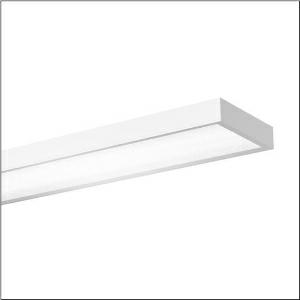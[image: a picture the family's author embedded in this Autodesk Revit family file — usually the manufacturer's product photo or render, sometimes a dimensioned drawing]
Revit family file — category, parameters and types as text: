
# Revit family: sport_31_51hs12dd4jca
name_source: partatom
category: Lighting Fixtures
units: mm (PartAtom-declared; Revit-internal decimal feet)

## family parameters
Cut with Voids When Loaded = No
Host = Face
Light Source = No
Part Type = Normal
Room Calculation Point = No
Round Connector Dimension = Use Diameter
Shared = No

## types (1)
- --- (1 x LED, 19720 lm, 146.2 W, 4000K)
    Apparent Load = 146 VA
    CIE Flux Codes = 65 89 97 100 100
    Color Rendering = 80
    Color Temperature = 4000K
    Default Elevation = 1800 mm
    Description = Sport 31, LED high bay luminaire, primary light control with reflector, of sheet steel, primary anti-glare with prismatic structure, of PC, primary optical cover: cover panel, of PC, light emission: direct distribution, primary light characteristic: symmetric, installation type: suspended mounting, recessed, surface-mounted, LED, rated luminous flux: 20.000lm, luminous efficacy: 137lm/W, light colour: 840, colour temperature: 4000K, control gear: DALI 2, with terminal, 5-pole, max. 2.5mm², mains connection: 220..240V, AC/DC, 50/60Hz, rated input power: 146W, housing, of sheet steel, traffic white (RAL 9016), length: 1.540mm, width: 415mm, height: 95mm, protection rating (complete): IP20, protection rating (lamp compartment, on room side): IP50, insulation class (complete): insulation class I (protective earthing), certification: CE, ENEC, UKCA, ball protection: ball impact resistant with ceiling mounting or chain suspension, impact resistance: IK08, permissible operating ambient temperature: -20..+35°C, standard: DIN 18032-3, EN 60598-2-22, packaging unit: 1 piece
    Height = 100 mm  [stored 0.328084 ft]
    Lamp = 1 x LED
    Lamp Light Flux = 19720 lm
    Lamp Power = 146.2 W
    Lamp count = 1
    Length = 1500 mm
    Luminous efficacy = 135 lm/W
    Manufacturer = Siteco
    ModVariant = No
    Model = 51HS12DD4JCA
    Mounting Place = Ceiling
    Mounting Type = Pendant
    Number of Poles = 1
    OnlyDefault = Yes
    Power Factor = 1
    Product Name = Sport 31
    Product group = LED high bay luminaire
    ProductGroupID = 903
    Protection Class = Protection class I
    Protection Degree = IP 20
    RLX_Detail_Level = 1
    RLX_Emergency_Light_Flux = 0 lm
    RLX_Emergency_Type = 0
    RLX_Emergency_Type_DB = No
    RlxData = <blob elided: 24129 chars, md5=a3e19410>
    Socket = socket
    Standby Power = 0 W
    System Light Flux = 19719 lm
    System Power = 146 W
    Type Comments = factory setting: luminous flux: 100 % | dim-lin: 254 | 610 mA
    Type Image = l_1006829.jpg
    URL = http://relux.com
    VarID = @adj_197098
    Voltage = 0 V
    Weight = 0.00 kg
    Width = 415 mm

note: [stored X ft] marks values corroborated as IEEE doubles in the binary element streams (Revit-internal decimal feet)

## geometry (parser evidence)
native form markers: Blend x4, Sweep x10
no freeform markers — native parametric forms only
